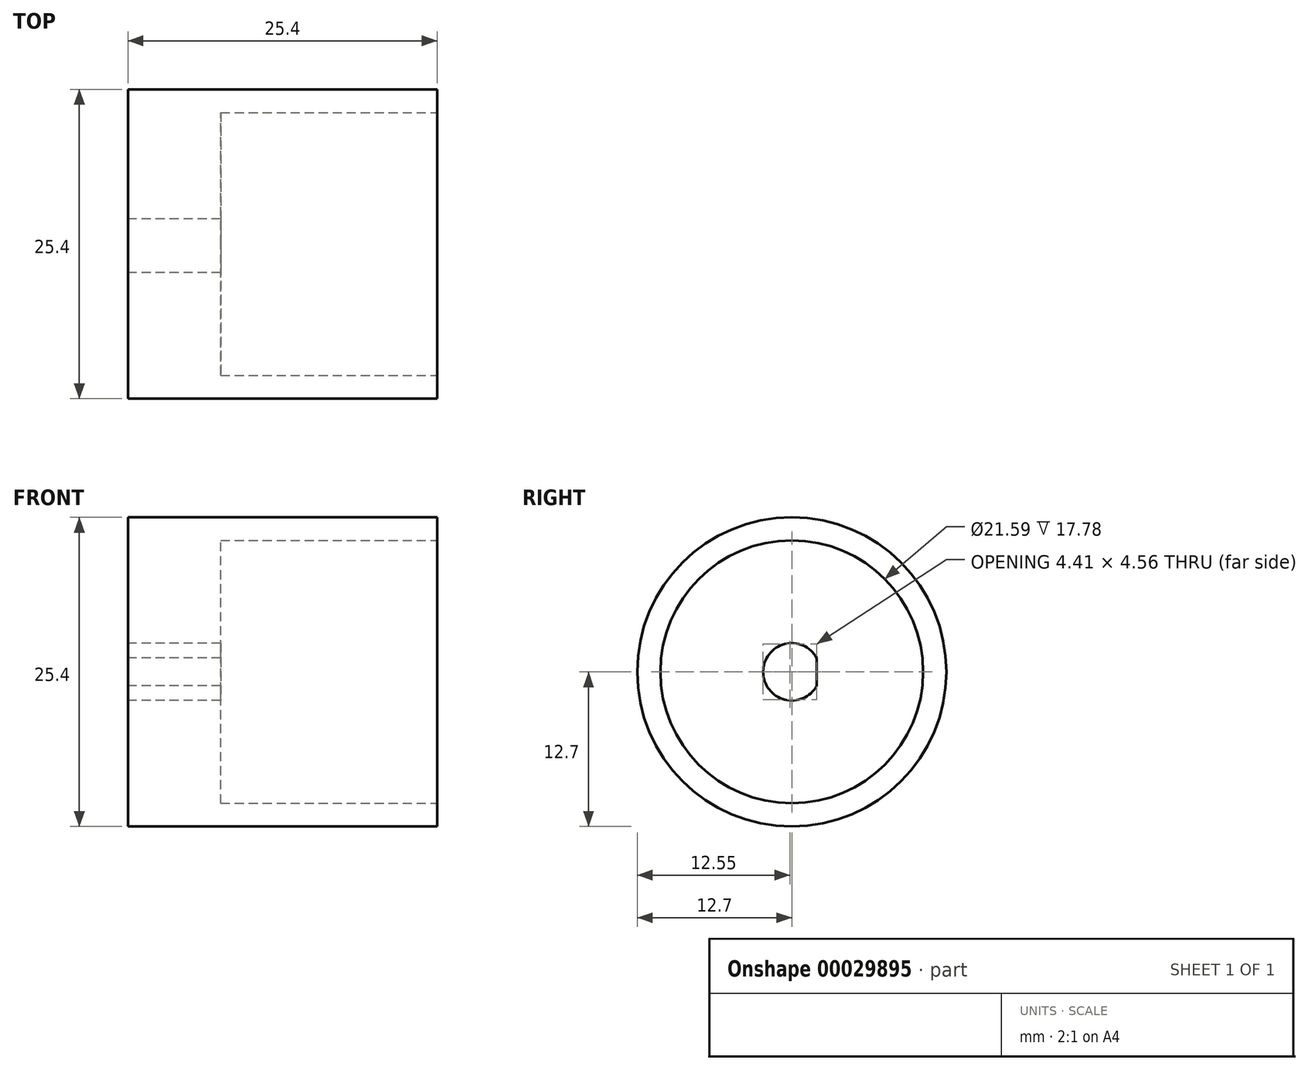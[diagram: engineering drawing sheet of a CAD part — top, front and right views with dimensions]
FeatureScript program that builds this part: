
annotation { "Feature Type Name" : "Feature", "Feature Type Description" : "" }
export const myFeature = defineFeature(function(context is Context, id is Id, definition is map)
    precondition{}
    {
        {
            var Q0;
            Q0=qCreatedBy(makeId("Right.planeOp"),FACE);
            var sketch = newSketch(context, id + "F0", { "sketchPlane" : qUnion([Q0])});
            skCircle(sketch, "E0", {"center": v(0, 0) * mm, "radius": 2.35 * mm});
            skCircle(sketch, "E1", {"center": v(0, 0) * mm, "radius": 12.7 * mm});
            skLineSegment(sketch, "E2", {"start": v(2.06, 1.15) * mm, "end": v(2.06, -1.15) * mm});
            skSolve(sketch);
        }
        {
            var Q0;
            Q0=qCreatedBy(makeId("Right.planeOp"),FACE);
            cPlane(context, id + "F1", {"entities" : qUnion([Q0]), "cplaneType" : CPlaneType.OFFSET, "offset" : 25.4 * mm, "width" : 152.4 * mm, "height" : 152.4 * mm});
        }
        {
            var Q0;
            Q0=qCreatedBy(id+"F1.planeOp",FACE);
            var sketch = newSketch(context, id + "F2", { "sketchPlane" : qUnion([Q0])});
            skPoint(sketch, "E3.0", {"position": v(0, 0) * mm});
            skCircle(sketch, "E4", {"center": v(0, 0) * mm, "radius": 12.7 * mm});
            skCircle(sketch, "E5", {"center": v(0, 0) * mm, "radius": 10.8 * mm});
            skSolve(sketch);
        }
        {
            var Q0;
            Q0=makeQuery(id+"F0.imprint","IMPRINT",FACE,{"disambiguationData":[TD([[makeQuery(id+"F0.imprint","IMPRINT",EDGE,{"derivedFrom":sQuery(id+"F0.wireOp",EDGE,"E0")}),-1.0]])]});
            var Q1;
            Q1=makeQuery(id+"F0.imprint","IMPRINT",FACE,{"disambiguationData":[TD([[makeQuery(id+"F0.imprint","IMPRINT",EDGE,{"derivedFrom":sQuery(id+"F0.wireOp",EDGE,"E0")}),1.0]])]});
            extrude(context, id + "F3", {"entities" : qUnion([Q0, Q1]), "depth" : 25.4 * mm});
        }
        {
            var Q0;
            Q0=makeQuery(id+"F2.imprint","IMPRINT",FACE,{"disambiguationData":[TD([[makeQuery(id+"F2.imprint","IMPRINT",EDGE,{"derivedFrom":sQuery(id+"F2.wireOp",EDGE,"E5")}),1.0]])]});
            extrude(context, id + "F4", {"entities" : qUnion([Q0]), "operationType" : NewBodyOperationType.REMOVE, "oppositeDirection" : true, "depth" : 30.48 * mm});
        }
        {
            var Q0;
            Q0=makeQuery(id+"F0.imprint","IMPRINT",FACE,{"disambiguationData":[TD([[makeQuery(id+"F0.imprint","IMPRINT",EDGE,{"derivedFrom":sQuery(id+"F0.wireOp",EDGE,"E0")}),-1.0]])]});
            extrude(context, id + "F5", {"entities" : qUnion([Q0]), "operationType" : NewBodyOperationType.ADD, "depth" : 5.08 * mm});
        }
        {
            var Q0;
            {var subQ0=sQuery(id+"F0.wireOp",EDGE,"E2");Q0=makeQuery(id+"F0.imprint","IMPRINT",FACE,{"disambiguationData":[TD([[makeQuery(id+"F0.imprint","IMPRINT",EDGE,{"derivedFrom":subQ0}),1.0]])]});}
            var Q1;
            Q1=makeQuery(id+"F0.imprint","IMPRINT",FACE,{"disambiguationData":[TD([[makeQuery(id+"F0.imprint","IMPRINT",EDGE,{"derivedFrom":sQuery(id+"F0.wireOp",EDGE,"E1")}),1.0]])]});
            extrude(context, id + "F6", {"entities" : qUnion([Q0, Q1]), "operationType" : NewBodyOperationType.ADD, "depth" : 7.62 * mm});
        }
    });
